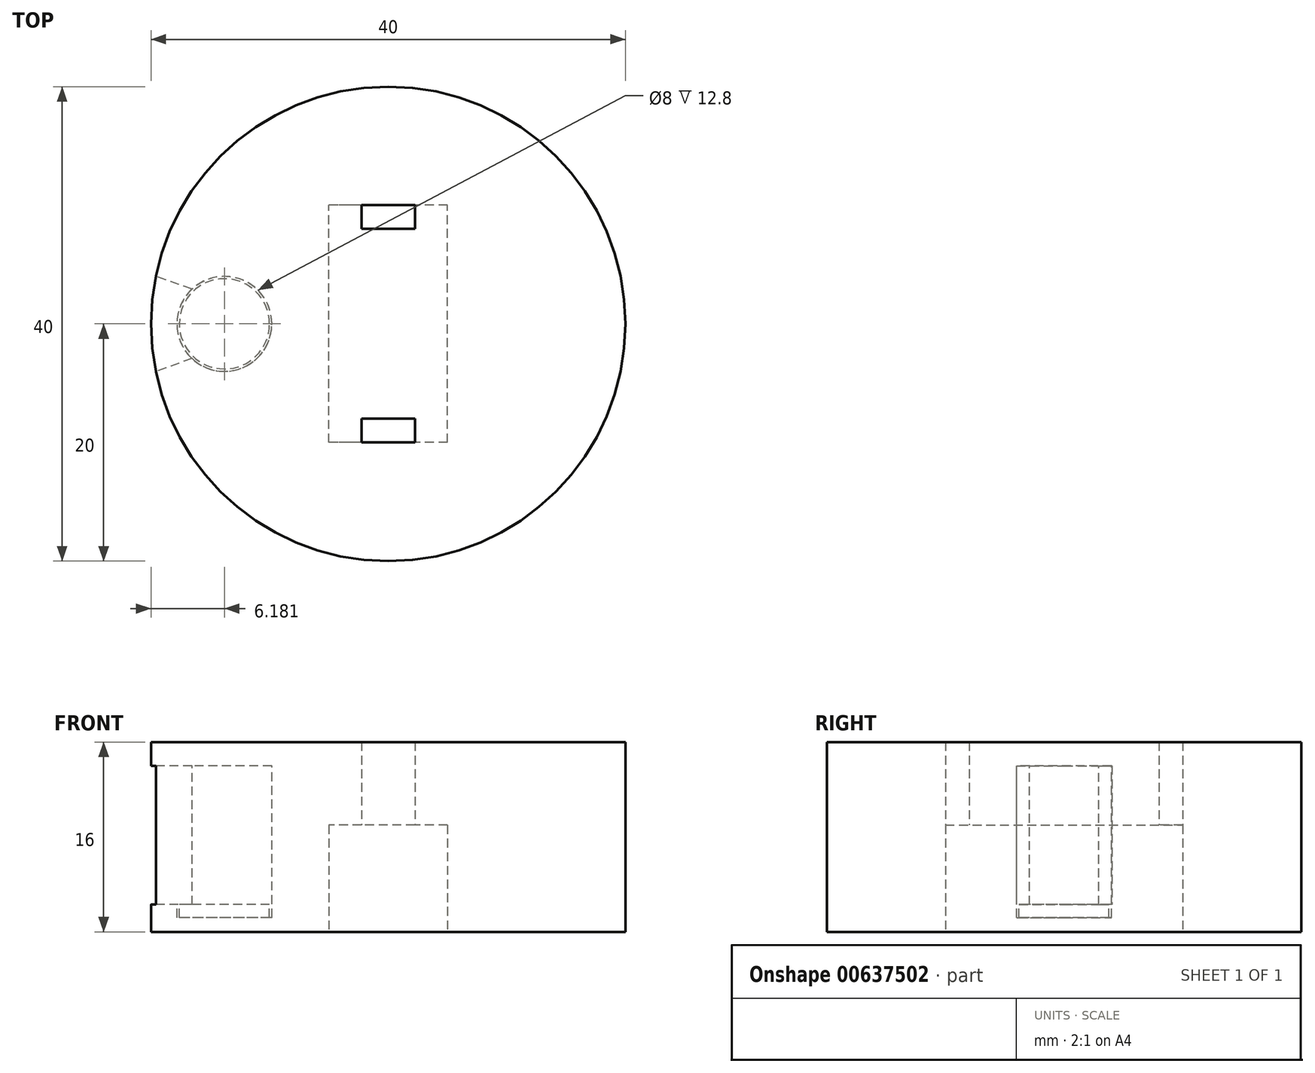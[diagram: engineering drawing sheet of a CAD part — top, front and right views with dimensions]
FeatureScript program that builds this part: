
annotation { "Feature Type Name" : "Feature", "Feature Type Description" : "" }
export const myFeature = defineFeature(function(context is Context, id is Id, definition is map)
    precondition{}
    {
        {
            var Q0;
            Q0=qCreatedBy(makeId("Top.planeOp"),FACE);
            var sketch = newSketch(context, id + "F0", { "sketchPlane" : qUnion([Q0])});
            skCircle(sketch, "E0", {"center": v(0, 0) * mm, "radius": 20 * mm});
            skSolve(sketch);
        }
        {
            var Q0;
            Q0=makeQuery(id+"F0.imprint","IMPRINT",FACE,{"disambiguationData":[TD([[makeQuery(id+"F0.imprint","IMPRINT",EDGE,{"derivedFrom":sQuery(id+"F0.wireOp",EDGE,"E0")}),1.0]])]});
            extrude(context, id + "F1", {"entities" : qUnion([Q0]), "depth" : 16 * mm, "offsetDistance" : 25 * mm});
        }
        {
            var Q0;
            Q0=makeQuery(id+"F1.opExtrude","CAP_FACE",FACE,{"disambiguationData":[OSD([sQuery(id+"F0.wireOp",EDGE,"E0")])],"isStart":true});
            var sketch = newSketch(context, id + "F2", { "sketchPlane" : qUnion([Q0])});
            skLineSegment(sketch, "E1.bottom", {"start": v(5, 10) * mm, "end": v(-5, 10) * mm});
            skLineSegment(sketch, "E1.top", {"start": v(5, -10) * mm, "end": v(-5, -10) * mm});
            skLineSegment(sketch, "E1.left", {"start": v(5, 10) * mm, "end": v(5, -10) * mm});
            skLineSegment(sketch, "E1.right", {"start": v(-5, 10) * mm, "end": v(-5, -10) * mm});
            skPoint(sketch, "E1.middle", {"position": v(0, 0) * mm});
            skSolve(sketch);
        }
        {
            var Q0;
            Q0=makeQuery(id+"F2.imprint","IMPRINT",FACE,{"disambiguationData":[TD([[makeQuery(id+"F2.imprint","IMPRINT",EDGE,{"derivedFrom":sQuery(id+"F2.wireOp",EDGE,"E1.bottom")}),1.0]])]});
            extrude(context, id + "F3", {"entities" : qUnion([Q0]), "operationType" : NewBodyOperationType.REMOVE, "oppositeDirection" : true, "depth" : 9 * mm, "offsetDistance" : 25 * mm});
        }
        {
            var Q0;
            Q0=makeQuery(id+"F3.boolean.opBoolean","COPY",FACE,{"derivedFrom":makeQuery(id+"F3.opExtrude","CAP_FACE",FACE,{"disambiguationData":[OSD([sQuery(id+"F2.wireOp",EDGE,"E1.bottom"),sQuery(id+"F2.wireOp",EDGE,"E1.top"),sQuery(id+"F2.wireOp",EDGE,"E1.left"),sQuery(id+"F2.wireOp",EDGE,"E1.right")])],"isStart":false})});
            var sketch = newSketch(context, id + "F4", { "sketchPlane" : qUnion([Q0])});
            skLineSegment(sketch, "E2", {"start": v(0, 10) * mm, "end": v(0, -10) * mm, "construction": true});
            skLineSegment(sketch, "E3.bottom", {"start": v(2.25, 10) * mm, "end": v(-2.25, 10) * mm});
            skLineSegment(sketch, "E3.top", {"start": v(2.25, 8) * mm, "end": v(-2.25, 8) * mm});
            skLineSegment(sketch, "E3.left", {"start": v(2.25, 10) * mm, "end": v(2.25, 8) * mm});
            skLineSegment(sketch, "E3.right", {"start": v(-2.25, 10) * mm, "end": v(-2.25, 8) * mm});
            skPoint(sketch, "E3.middle", {"position": v(0, 9) * mm});
            skLineSegment(sketch, "E4.MirrorCS", {"start": v(2.25, 10) * mm, "end": v(6.75, 10) * mm, "construction": true});
            skLineSegment(sketch, "E5", {"start": v(0, 0) * mm, "end": v(1.88, 0) * mm, "construction": true});
            skLineSegment(sketch, "E6.MirrorCS", {"start": v(2.25, -10) * mm, "end": v(2.25, -8) * mm});
            skLineSegment(sketch, "E7.MirrorCS", {"start": v(2.25, -10) * mm, "end": v(-2.25, -10) * mm});
            skLineSegment(sketch, "E8.MirrorCS", {"start": v(2.25, -8) * mm, "end": v(-2.25, -8) * mm});
            skLineSegment(sketch, "E9.MirrorCS", {"start": v(-2.25, -10) * mm, "end": v(-2.25, -8) * mm});
            skSolve(sketch);
        }
        {
            var Q0;
            Q0 = qSketchRegion(id + "F4", true);
            extrude(context, id + "F5", {"entities" : qUnion([Q0]), "operationType" : NewBodyOperationType.REMOVE, "endBound" : BoundingType.THROUGH_ALL, "oppositeDirection" : true, "depth" : 25 * mm, "offsetDistance" : 25 * mm});
        }
        {
            var Q0;
            Q0=makeQuery(id+"F1.opExtrude","CAP_FACE",FACE,{"disambiguationData":[OSD([sQuery(id+"F0.wireOp",EDGE,"E0")])],"isStart":false});
            cPlane(context, id + "F6", {"entities" : qUnion([Q0]), "cplaneType" : CPlaneType.OFFSET, "offset" : 2 * mm, "oppositeDirection" : true, "width" : 150 * mm, "height" : 150 * mm});
        }
        {
            var Q0;
            Q0=qCreatedBy(id+"F6.planeOp",FACE);
            var sketch = newSketch(context, id + "F7", { "sketchPlane" : qUnion([Q0])});
            skLineSegment(sketch, "E10", {"start": v(0, 0) * mm, "end": v(-20, 0) * mm, "construction": true});
            skCircle(sketch, "E11", {"center": v(-13.82, 0) * mm, "radius": 4 * mm});
            skCircle(sketch, "E12", {"center": v(-13.82, 0) * mm, "radius": 3.8 * mm});
            skSolve(sketch);
        }
        {
            var Q0;
            Q0 = qSketchRegion(id + "F7", true);
            extrude(context, id + "F8", {"entities" : qUnion([Q0]), "operationType" : NewBodyOperationType.REMOVE, "oppositeDirection" : true, "depth" : 12.8 * mm, "offsetDistance" : 25 * mm});
        }
        {
            var Q0;
            Q0=qCreatedBy(id+"F6.planeOp",FACE);
            var sketch = newSketch(context, id + "F9", { "sketchPlane" : qUnion([Q0])});
            skArc(sketch, "E13.0", {"start": v(-16.55, -2.92) * mm, "mid": v(-9.82, 0) * mm, "end": v(-16.55, 2.92) * mm});
            skLineSegment(sketch, "E14", {"start": v(-16.55, 2.92) * mm, "end": v(-26.82, 6.66) * mm});
            skLineSegment(sketch, "E15", {"start": v(-26.82, 6.66) * mm, "end": v(-26.82, 0) * mm});
            skLineSegment(sketch, "E16", {"start": v(-26.82, 0) * mm, "end": v(-17.82, 0) * mm, "construction": true});
            skLineSegment(sketch, "E17.MirrorCS", {"start": v(-16.55, -2.92) * mm, "end": v(-26.82, -6.66) * mm});
            skLineSegment(sketch, "E18.MirrorCS", {"start": v(-26.82, -6.66) * mm, "end": v(-26.82, 0) * mm});
            skSolve(sketch);
        }
        {
            var Q0;
            Q0 = qSketchRegion(id + "F9", true);
            extrude(context, id + "F10", {"entities" : qUnion([Q0]), "operationType" : NewBodyOperationType.REMOVE, "oppositeDirection" : true, "depth" : 11.7 * mm, "offsetDistance" : 25 * mm});
        }
    });
